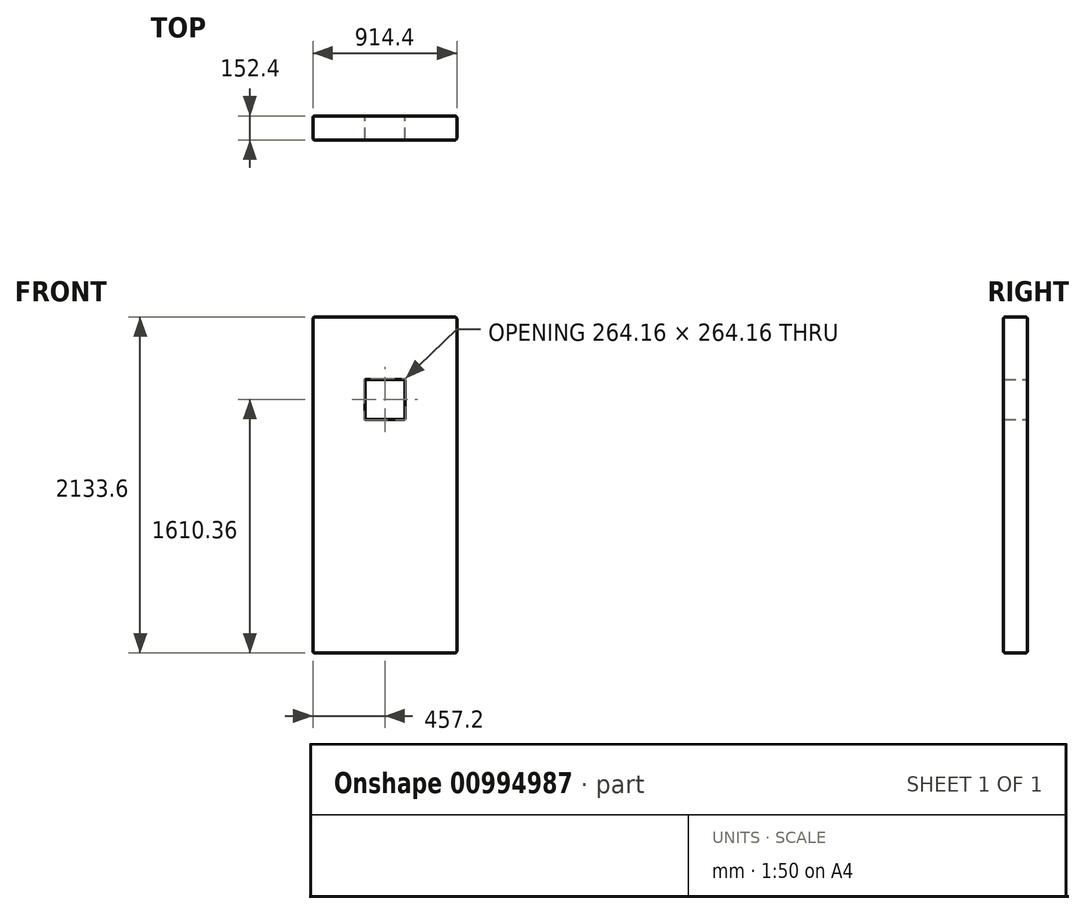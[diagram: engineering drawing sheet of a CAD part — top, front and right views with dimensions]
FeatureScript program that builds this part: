
annotation { "Feature Type Name" : "Feature", "Feature Type Description" : "" }
export const myFeature = defineFeature(function(context is Context, id is Id, definition is map)
    precondition{}
    {
        {
            var Q0;
            Q0=qCreatedBy(makeId("Front.planeOp"),FACE);
            var sketch = newSketch(context, id + "F0", { "sketchPlane" : qUnion([Q0])});
            skLineSegment(sketch, "E0", {"start": v(0, 0) * mm, "end": v(914.4, 0) * mm});
            skLineSegment(sketch, "E1", {"start": v(914.4, 0) * mm, "end": v(914.4, 2133.6) * mm});
            skLineSegment(sketch, "E2", {"start": v(0, 0) * mm, "end": v(0, 2133.6) * mm});
            skLineSegment(sketch, "E3", {"start": v(0, 2133.6) * mm, "end": v(914.4, 2133.6) * mm});
            skLineSegment(sketch, "E4", {"start": v(457.2, 1737.36) * mm, "end": v(584.2, 1737.36) * mm});
            skLineSegment(sketch, "E5", {"start": v(584.2, 1737.36) * mm, "end": v(584.2, 1483.36) * mm});
            skLineSegment(sketch, "E6", {"start": v(584.2, 1483.36) * mm, "end": v(330.2, 1483.36) * mm});
            skLineSegment(sketch, "E7", {"start": v(330.2, 1483.36) * mm, "end": v(330.2, 1737.36) * mm});
            skLineSegment(sketch, "E8", {"start": v(330.2, 1737.36) * mm, "end": v(457.2, 1737.36) * mm});
            skSolve(sketch);
        }
        {
            var Q0;
            Q0 = qSketchRegion(id + "F0", true);
            extrude(context, id + "F1", {"entities" : qUnion([Q0]), "depth" : 152.4 * mm, "offsetDistance" : 25.4 * mm});
        }
        {
            var Q0;
            Q0=makeQuery(id+"F1.opExtrude","CAP_EDGE",EDGE,{"disambiguationData":[OSD([sQuery(id+"F0.wireOp",EDGE,"E3")])],"isStart":false});
            var Q1;
            Q1=makeQuery(id+"F1.opExtrude","CAP_EDGE",EDGE,{"disambiguationData":[OSD([sQuery(id+"F0.wireOp",EDGE,"E1")])],"isStart":false});
            var Q2;
            Q2=makeQuery(id+"F1.opExtrude","SWEPT_EDGE",EDGE,{"disambiguationData":[OSD([sQuery(id+"F0.wireOp",EDGE,"E1"),sQuery(id+"F0.wireOp",EDGE,"E3")])]});
            var Q3;
            Q3=makeQuery(id+"F1.opExtrude","CAP_EDGE",EDGE,{"disambiguationData":[OSD([sQuery(id+"F0.wireOp",EDGE,"E3")])],"isStart":true});
            var Q4;
            Q4=makeQuery(id+"F1.opExtrude","CAP_EDGE",EDGE,{"disambiguationData":[OSD([sQuery(id+"F0.wireOp",EDGE,"E1")])],"isStart":true});
            var Q5;
            Q5=makeQuery(id+"F1.opExtrude","SWEPT_EDGE",EDGE,{"disambiguationData":[OSD([sQuery(id+"F0.wireOp",EDGE,"E0"),sQuery(id+"F0.wireOp",EDGE,"E1")])]});
            var Q6;
            Q6=makeQuery(id+"F1.opExtrude","CAP_EDGE",EDGE,{"disambiguationData":[OSD([sQuery(id+"F0.wireOp",EDGE,"E0")])],"isStart":false});
            var Q7;
            Q7=makeQuery(id+"F1.opExtrude","CAP_EDGE",EDGE,{"disambiguationData":[OSD([sQuery(id+"F0.wireOp",EDGE,"E2")])],"isStart":false});
            var Q8;
            Q8=makeQuery(id+"F1.opExtrude","CAP_EDGE",EDGE,{"disambiguationData":[OSD([sQuery(id+"F0.wireOp",EDGE,"E0")])],"isStart":true});
            var Q9;
            Q9=makeQuery(id+"F1.opExtrude","CAP_EDGE",EDGE,{"disambiguationData":[OSD([sQuery(id+"F0.wireOp",EDGE,"E2")])],"isStart":true});
            var Q10;
            Q10=makeQuery(id+"F1.opExtrude","SWEPT_EDGE",EDGE,{"disambiguationData":[OSD([sQuery(id+"F0.wireOp",EDGE,"E0"),sQuery(id+"F0.wireOp",EDGE,"E2")])]});
            var Q11;
            Q11=makeQuery(id+"F1.opExtrude","SWEPT_EDGE",EDGE,{"disambiguationData":[OSD([sQuery(id+"F0.wireOp",EDGE,"E2"),sQuery(id+"F0.wireOp",EDGE,"E3")])]});
            fillet(context, id + "F2", {"entities" : qUnion([Q0, Q1, Q2, Q3, Q4, Q5, Q6, Q7, Q8, Q9, Q10, Q11]), "radius" : 12.7 * mm, "tangentPropagation" : true, "allowEdgeOverflow" : false});
        }
        {
            var Q0;
            Q0=makeQuery(id+"F1.opExtrude","SWEPT_EDGE",EDGE,{"disambiguationData":[OSD([sQuery(id+"F0.wireOp",EDGE,"B1n5sGBE-GVCG-1Qw1-RsPh-abCOSR9Aqsa2"),sQuery(id+"F0.wireOp",EDGE,"bz11KPA7-BjQu-1gEp-GoPZ-CLYwN1VP5e7W")])]});
            var Q1;
            Q1=makeQuery(id+"F1.opExtrude","CAP_EDGE",EDGE,{"disambiguationData":[OSD([sQuery(id+"F0.wireOp",EDGE,"B1n5sGBE-GVCG-1Qw1-RsPh-abCOSR9Aqsa2")])],"isStart":false});
            var Q2;
            Q2=makeQuery(id+"F1.opExtrude","CAP_EDGE",EDGE,{"disambiguationData":[OSD([sQuery(id+"F0.wireOp",EDGE,"bz11KPA7-BjQu-1gEp-GoPZ-CLYwN1VP5e7W")])],"isStart":false});
            var Q3;
            Q3=makeQuery(id+"F1.opExtrude","SWEPT_EDGE",EDGE,{"disambiguationData":[OSD([sQuery(id+"F0.wireOp",EDGE,"B1n5sGBE-GVCG-1Qw1-RsPh-abCOSR9Aqsa2"),sQuery(id+"F0.wireOp",EDGE,"RZO8sjAf-iQLw-44xb-1Qy3-eyq2yfKunQak")])]});
            var Q4;
            Q4=makeQuery(id+"F1.opExtrude","CAP_EDGE",EDGE,{"disambiguationData":[OSD([sQuery(id+"F0.wireOp",EDGE,"RZO8sjAf-iQLw-44xb-1Qy3-eyq2yfKunQak")])],"isStart":false});
            var Q5;
            Q5=makeQuery(id+"F1.opExtrude","SWEPT_FACE",FACE,{"disambiguationData":[OSD([sQuery(id+"F0.wireOp",EDGE,"PVnPVhx5-1lOt-NvAK-kpe7-autbysIbxb4k")])]});
            var Q6;
            Q6=makeQuery(id+"F1.opExtrude","CAP_EDGE",EDGE,{"disambiguationData":[OSD([sQuery(id+"F0.wireOp",EDGE,"E6")])],"isStart":false});
            var Q7;
            Q7=makeQuery(id+"F1.opExtrude","CAP_EDGE",EDGE,{"disambiguationData":[OSD([sQuery(id+"F0.wireOp",EDGE,"E7")])],"isStart":false});
            var Q8;
            Q8=makeQuery(id+"F1.opExtrude","CAP_EDGE",EDGE,{"disambiguationData":[OSD([sQuery(id+"F0.wireOp",EDGE,"E4"),sQuery(id+"F0.wireOp",EDGE,"E8")])],"isStart":false});
            var Q9;
            Q9=makeQuery(id+"F1.opExtrude","CAP_EDGE",EDGE,{"disambiguationData":[OSD([sQuery(id+"F0.wireOp",EDGE,"E6")])],"isStart":true});
            var Q10;
            Q10=makeQuery(id+"F1.opExtrude","CAP_EDGE",EDGE,{"disambiguationData":[OSD([sQuery(id+"F0.wireOp",EDGE,"E7")])],"isStart":true});
            var Q11;
            Q11=makeQuery(id+"F1.opExtrude","CAP_EDGE",EDGE,{"disambiguationData":[OSD([sQuery(id+"F0.wireOp",EDGE,"E5")])],"isStart":true});
            var Q12;
            Q12=makeQuery(id+"F1.opExtrude","CAP_EDGE",EDGE,{"disambiguationData":[OSD([sQuery(id+"F0.wireOp",EDGE,"E4"),sQuery(id+"F0.wireOp",EDGE,"E8")])],"isStart":true});
            var Q13;
            Q13=makeQuery(id+"F1.opExtrude","CAP_EDGE",EDGE,{"disambiguationData":[OSD([sQuery(id+"F0.wireOp",EDGE,"E5")])],"isStart":false});
            var Q14;
            Q14=makeQuery(id+"F1.opExtrude","SWEPT_EDGE",EDGE,{"disambiguationData":[OSD([sQuery(id+"F0.wireOp",EDGE,"E5"),sQuery(id+"F0.wireOp",EDGE,"E6")])]});
            var Q15;
            Q15=makeQuery(id+"F1.opExtrude","SWEPT_EDGE",EDGE,{"disambiguationData":[OSD([sQuery(id+"F0.wireOp",EDGE,"E6"),sQuery(id+"F0.wireOp",EDGE,"E7")])]});
            var Q16;
            Q16=makeQuery(id+"F1.opExtrude","SWEPT_EDGE",EDGE,{"disambiguationData":[OSD([sQuery(id+"F0.wireOp",EDGE,"E7"),sQuery(id+"F0.wireOp",EDGE,"E8")])]});
            var Q17;
            Q17=makeQuery(id+"F1.opExtrude","SWEPT_EDGE",EDGE,{"disambiguationData":[OSD([sQuery(id+"F0.wireOp",EDGE,"E4"),sQuery(id+"F0.wireOp",EDGE,"E5")])]});
            fillet(context, id + "F3", {"entities" : qUnion([Q0, Q1, Q2, Q3, Q4, Q5, Q6, Q7, Q8, Q9, Q10, Q11, Q12, Q13, Q14, Q15, Q16, Q17]), "radius" : 5.08 * mm, "tangentPropagation" : true, "allowEdgeOverflow" : false});
        }
    });
